# Revit family: Lavatory-Bradley_Corp-Verge-LVQ-2_Station
name_source: partatom
category: Plumbing Fixtures
revit_build: Autodesk Revit 2014 (Build: 20140709_2115(x64)
units: mm (PartAtom-declared; Revit-internal decimal feet)

## types (1)
- LVQ-2
    ADA Compliant = Yes
    Assembly Code = D2010300
    Depth = 21"
    Description = Verge™ Lavatory System w/Washbar Technology – LVQ Series, Two Station
    Installation Type = Wall Hung
    Length = 30"
    Manufacturer = Bradley Corporation
    MasterFormat Number = 22 42 16
    MasterFormat Title = Commercial Lavatories and Sinks
    Model = LVQD2
    OmniClass Table 21 Number = 21-04 20 10 60
    OmniClass Table 21 Title = Plumbing Fixtures
    OmniClass Table 23 Number = 23-31 13 00
    OmniClass Table 23 Title = Sink/Lavatories
    Product Page URL = http://info.bradleycorp.com
    Product Tech Data URL - English = https://www.bradleycorp.com
    Specifications URL = https://www.bradleycorp.com
    URL = http://bradleycorp.com

## geometry (parser evidence)
native form markers: Sweep x7
no freeform markers — native parametric forms only
